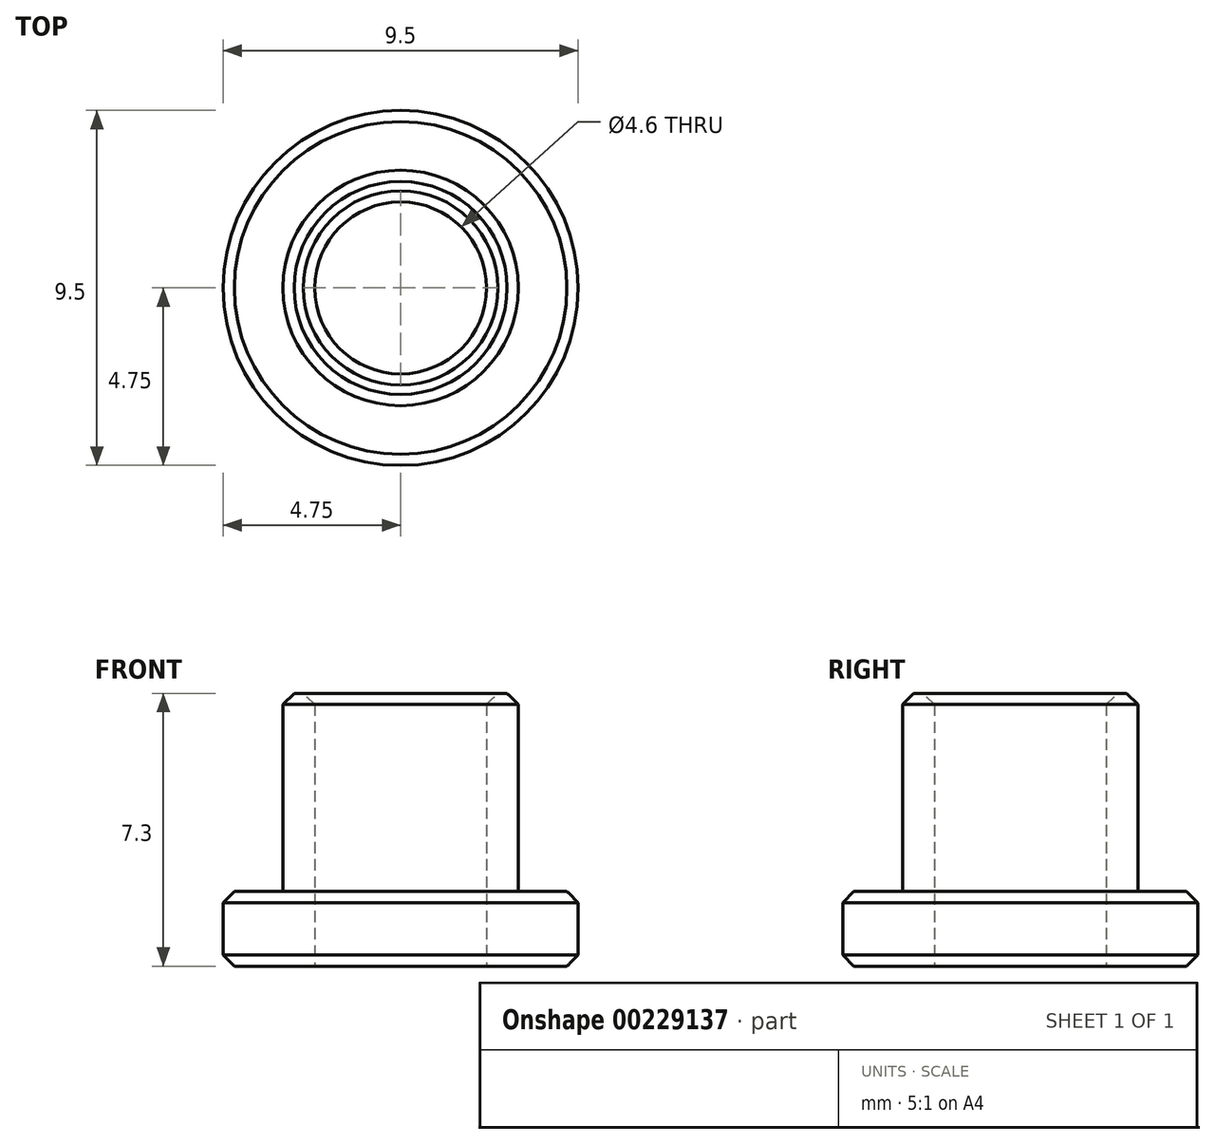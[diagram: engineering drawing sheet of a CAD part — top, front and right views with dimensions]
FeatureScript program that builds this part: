
annotation { "Feature Type Name" : "Feature", "Feature Type Description" : "" }
export const myFeature = defineFeature(function(context is Context, id is Id, definition is map)
    precondition{}
    {
        {
            var Q0;
            Q0=qCreatedBy(makeId("Top.planeOp"),FACE);
            var sketch = newSketch(context, id + "F0", { "sketchPlane" : qUnion([Q0])});
            skCircle(sketch, "E0", {"center": v(0, 0) * mm, "radius": 4.75 * mm});
            skSolve(sketch);
        }
        {
            var Q0;
            Q0 = qSketchRegion(id + "F0", true);
            extrude(context, id + "F1", {"entities" : qUnion([Q0]), "depth" : 2 * mm});
        }
        {
            var Q0;
            Q0=makeQuery(id+"F1.opExtrude","CAP_FACE",FACE,{"disambiguationData":[OSD([sQuery(id+"F0.wireOp",EDGE,"E0")])],"isStart":false});
            var sketch = newSketch(context, id + "F2", { "sketchPlane" : qUnion([Q0])});
            skCircle(sketch, "E1", {"center": v(0, 0) * mm, "radius": 3.15 * mm});
            skSolve(sketch);
        }
        {
            var Q0;
            Q0 = qSketchRegion(id + "F2", true);
            extrude(context, id + "F3", {"entities" : qUnion([Q0]), "operationType" : NewBodyOperationType.ADD, "depth" : 5.3 * mm});
        }
        {
            var Q0;
            Q0=makeQuery(id+"F1.opExtrude","CAP_FACE",FACE,{"disambiguationData":[OSD([sQuery(id+"F0.wireOp",EDGE,"E0")])],"isStart":true});
            var sketch = newSketch(context, id + "F4", { "sketchPlane" : qUnion([Q0])});
            skCircle(sketch, "E2", {"center": v(0, 0) * mm, "radius": 2.3 * mm});
            skSolve(sketch);
        }
        {
            var Q0;
            Q0 = qSketchRegion(id + "F4", true);
            extrude(context, id + "F5", {"entities" : qUnion([Q0]), "operationType" : NewBodyOperationType.REMOVE, "endBound" : BoundingType.THROUGH_ALL, "oppositeDirection" : true, "depth" : 25 * mm});
        }
        {
            var Q0;
            Q0=makeQuery(id+"F1.opExtrude","CAP_EDGE",EDGE,{"disambiguationData":[OSD([sQuery(id+"F0.wireOp",EDGE,"E0")])],"isStart":true});
            var Q1;
            Q1=makeQuery(id+"F5.boolean.opBoolean","COPY",EDGE,{"derivedFrom":makeQuery(id+"F5.opExtrude","CAP_EDGE",EDGE,{"disambiguationData":[OSD([sQuery(id+"F4.wireOp",EDGE,"E2")])],"isStart":true})});
            var Q2;
            Q2=makeQuery(id+"F5.boolean.opBoolean","INTERSECT",EDGE,{"derivedFrom":[makeQuery(id+"F3.opExtrude","CAP_FACE",FACE,{"disambiguationData":[OSD([sQuery(id+"F2.wireOp",EDGE,"E1")])],"isStart":false}),makeQuery(id+"F5.opExtrude","SWEPT_FACE",FACE,{"disambiguationData":[OSD([sQuery(id+"F4.wireOp",EDGE,"E2")])]})]});
            var Q3;
            Q3=makeQuery(id+"F3.opExtrude","CAP_EDGE",EDGE,{"disambiguationData":[OSD([sQuery(id+"F2.wireOp",EDGE,"E1")])],"isStart":false});
            var Q4;
            Q4=makeQuery(id+"F1.opExtrude","CAP_EDGE",EDGE,{"disambiguationData":[OSD([sQuery(id+"F0.wireOp",EDGE,"E0")])],"isStart":false});
            chamfer(context, id + "F6", {"entities" : qUnion([Q0, Q1, Q2, Q3, Q4]), "width" : .3 * mm, "tangentPropagation" : true});
        }
    });
